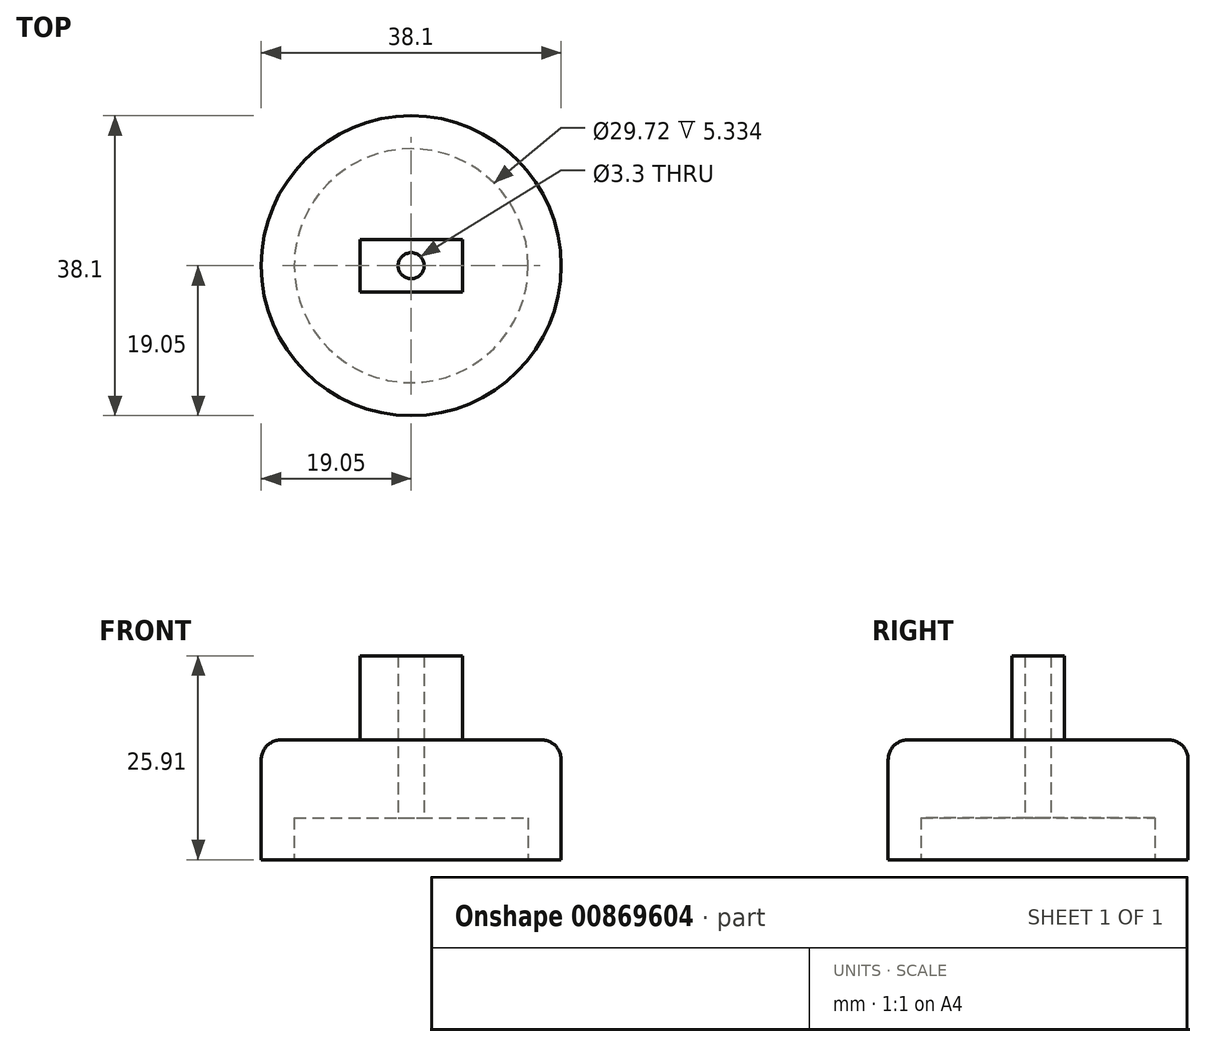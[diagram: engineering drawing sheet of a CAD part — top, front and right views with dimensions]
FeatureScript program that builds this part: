
annotation { "Feature Type Name" : "Feature", "Feature Type Description" : "" }
export const myFeature = defineFeature(function(context is Context, id is Id, definition is map)
    precondition{}
    {
        {
            var Q0;
            Q0=qCreatedBy(makeId("Top.planeOp"),FACE);
            var sketch = newSketch(context, id + "F0", { "sketchPlane" : qUnion([Q0])});
            skLineSegment(sketch, "E0.bottom", {"start": v(-6.5, 3.33) * mm, "end": v(6.5, 3.33) * mm});
            skLineSegment(sketch, "E0.top", {"start": v(-6.5, -3.33) * mm, "end": v(6.5, -3.33) * mm});
            skLineSegment(sketch, "E0.left", {"start": v(-6.5, 3.33) * mm, "end": v(-6.5, -3.33) * mm});
            skLineSegment(sketch, "E0.right", {"start": v(6.5, 3.33) * mm, "end": v(6.5, -3.33) * mm});
            skPoint(sketch, "E0.middle", {"position": v(0, 0) * mm});
            skSolve(sketch);
        }
        {
            var Q0;
            Q0 = qSketchRegion(id + "F0", true);
            extrude(context, id + "F1", {"entities" : qUnion([Q0]), "depth" : 10.67 * mm, "offsetDistance" : 25.4 * mm});
        }
        {
            var Q0;
            Q0=makeQuery(id+"F1.opExtrude","CAP_FACE",FACE,{"disambiguationData":[OSD([sQuery(id+"F0.wireOp",EDGE,"E0.bottom"),sQuery(id+"F0.wireOp",EDGE,"E0.top"),sQuery(id+"F0.wireOp",EDGE,"E0.left"),sQuery(id+"F0.wireOp",EDGE,"E0.right")])],"isStart":true});
            var sketch = newSketch(context, id + "F2", { "sketchPlane" : qUnion([Q0])});
            skCircle(sketch, "E1", {"center": v(0, 0) * mm, "radius": 19.05 * mm});
            skSolve(sketch);
        }
        {
            var Q0;
            Q0 = qSketchRegion(id + "F2", true);
            extrude(context, id + "F3", {"entities" : qUnion([Q0]), "operationType" : NewBodyOperationType.ADD, "depth" : 15.24 * mm, "offsetDistance" : 25.4 * mm});
        }
        {
            var Q0;
            Q0=makeQuery(id+"F3.opExtrude","CAP_EDGE",EDGE,{"disambiguationData":[OSD([sQuery(id+"F2.wireOp",EDGE,"E1")])],"isStart":true});
            fillet(context, id + "F4", {"entities" : qUnion([Q0]), "radius" : 2.54 * mm, "tangentPropagation" : true, "allowEdgeOverflow" : false});
        }
        {
            var Q0;
            Q0=makeQuery(id+"F3.opExtrude","CAP_FACE",FACE,{"disambiguationData":[OSD([sQuery(id+"F2.wireOp",EDGE,"E1")])],"isStart":false});
            var sketch = newSketch(context, id + "F5", { "sketchPlane" : qUnion([Q0])});
            skCircle(sketch, "E2", {"center": v(0, 0) * mm, "radius": 14.86 * mm});
            skSolve(sketch);
        }
        {
            var Q0;
            Q0 = qSketchRegion(id + "F5", true);
            extrude(context, id + "F6", {"entities" : qUnion([Q0]), "operationType" : NewBodyOperationType.REMOVE, "oppositeDirection" : true, "depth" : 5.33 * mm, "offsetDistance" : 25.4 * mm});
        }
        {
            var Q0;
            Q0=makeQuery(id+"F6.boolean.opBoolean","COPY",FACE,{"derivedFrom":makeQuery(id+"F6.opExtrude","CAP_FACE",FACE,{"disambiguationData":[OSD([sQuery(id+"F5.wireOp",EDGE,"E2")])],"isStart":false})});
            var sketch = newSketch(context, id + "F7", { "sketchPlane" : qUnion([Q0])});
            skCircle(sketch, "E3", {"center": v(0, 0) * mm, "radius": 1.65 * mm});
            skSolve(sketch);
        }
        {
            var Q0;
            Q0 = qSketchRegion(id + "F7", true);
            extrude(context, id + "F8", {"entities" : qUnion([Q0]), "operationType" : NewBodyOperationType.REMOVE, "oppositeDirection" : true, "depth" : 21.59 * mm, "offsetDistance" : 25.4 * mm});
        }
    });
